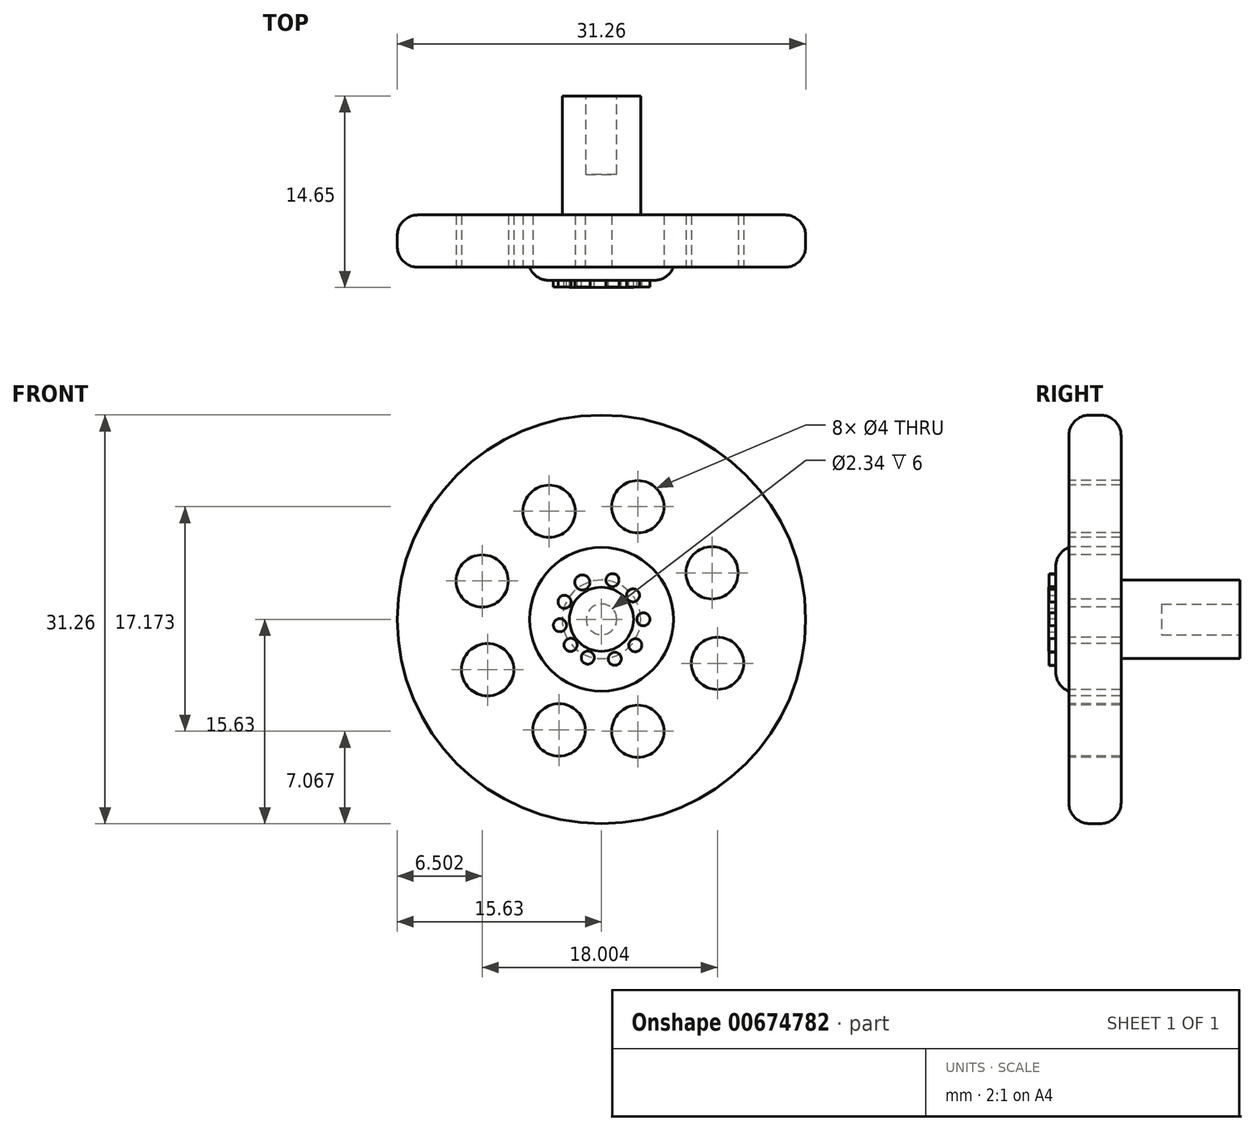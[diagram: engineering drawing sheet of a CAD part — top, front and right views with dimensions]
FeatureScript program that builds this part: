
annotation { "Feature Type Name" : "Feature", "Feature Type Description" : "" }
export const myFeature = defineFeature(function(context is Context, id is Id, definition is map)
    precondition{}
    {
        {
            var Q0;
            Q0=qCreatedBy(makeId("Front.planeOp"),FACE);
            var sketch = newSketch(context, id + "F0", { "sketchPlane" : qUnion([Q0])});
            skCircle(sketch, "E0", {"center": v(0, 0) * mm, "radius": 15.62 * mm});
            skSolve(sketch);
        }
        {
            var Q0;
            Q0 = qSketchRegion(id + "F0", true);
            extrude(context, id + "F1", {"entities" : qUnion([Q0]), "depth" : 4 * mm, "offsetDistance" : 25.4 * mm});
        }
        {
            var Q0;
            Q0=makeQuery(id+"F1.opExtrude","CAP_FACE",FACE,{"disambiguationData":[OSD([sQuery(id+"F0.wireOp",EDGE,"E0")])],"isStart":false});
            var sketch = newSketch(context, id + "F2", { "sketchPlane" : qUnion([Q0])});
            skCircle(sketch, "E1", {"center": v(0, 0) * mm, "radius": 2.45 * mm});
            skSolve(sketch);
        }
        {
            var Q0;
            Q0=makeQuery(id+"F2.imprint","IMPRINT",FACE,{"disambiguationData":[TD([[makeQuery(id+"F2.imprint","IMPRINT",EDGE,{"derivedFrom":sQuery(id+"F2.wireOp",EDGE,"E1")}),1.0]])]});
            extrude(context, id + "F3", {"entities" : qUnion([Q0]), "operationType" : NewBodyOperationType.ADD, "depth" : 1.55 * mm, "offsetDistance" : 25.4 * mm});
        }
        {
            var Q0;
            Q0=makeQuery(id+"F1.opExtrude","CAP_FACE",FACE,{"disambiguationData":[OSD([sQuery(id+"F0.wireOp",EDGE,"E0")])],"isStart":true});
            var sketch = newSketch(context, id + "F4", { "sketchPlane" : qUnion([Q0])});
            skCircle(sketch, "E2", {"center": v(0, 0) * mm, "radius": 3 * mm});
            skSolve(sketch);
        }
        {
            var Q0;
            Q0=makeQuery(id+"F4.imprint","IMPRINT",FACE,{"disambiguationData":[TD([[makeQuery(id+"F4.imprint","IMPRINT",EDGE,{"derivedFrom":sQuery(id+"F4.wireOp",EDGE,"E2")}),1.0]])]});
            extrude(context, id + "F5", {"entities" : qUnion([Q0]), "operationType" : NewBodyOperationType.ADD, "depth" : 9.1 * mm, "offsetDistance" : 25.4 * mm});
        }
        {
            var Q0;
            Q0=makeQuery(id+"F5.opExtrude","CAP_FACE",FACE,{"disambiguationData":[OSD([sQuery(id+"F4.wireOp",EDGE,"E2")])],"isStart":false});
            var sketch = newSketch(context, id + "F6", { "sketchPlane" : qUnion([Q0])});
            skCircle(sketch, "E3", {"center": v(0, 0) * mm, "radius": 1.17 * mm});
            skSolve(sketch);
        }
        {
            var Q0;
            Q0=makeQuery(id+"F6.imprint","IMPRINT",FACE,{"disambiguationData":[TD([[makeQuery(id+"F6.imprint","IMPRINT",EDGE,{"derivedFrom":sQuery(id+"F6.wireOp",EDGE,"E3")}),1.0]])]});
            var Q1;
            Q1=sQuery(id+"F6.wireOp",EDGE,"E3");
            extrude(context, id + "F7", {"entities" : qUnion([Q0]), "operationType" : NewBodyOperationType.REMOVE, "surfaceEntities" : qUnion([Q1]), "oppositeDirection" : true, "depth" : 6 * mm, "offsetDistance" : 25.4 * mm});
        }
        {
            var Q0;
            Q0=makeQuery(id+"F1.opExtrude","CAP_FACE",FACE,{"disambiguationData":[OSD([sQuery(id+"F0.wireOp",EDGE,"E0")])],"isStart":false});
            var sketch = newSketch(context, id + "F8", { "sketchPlane" : qUnion([Q0])});
            skCircle(sketch, "E4", {"center": v(0, 0) * mm, "radius": 5.5 * mm});
            skSolve(sketch);
        }
        {
            var Q0;
            Q0 = qSketchRegion(id + "F8", true);
            extrude(context, id + "F9", {"entities" : qUnion([Q0]), "operationType" : NewBodyOperationType.ADD, "depth" : 1 * mm, "offsetDistance" : 25.4 * mm});
        }
        {
            var Q0;
            Q0=makeQuery(id+"F1.opExtrude","CAP_EDGE",EDGE,{"disambiguationData":[OSD([sQuery(id+"F0.wireOp",EDGE,"E0")])],"isStart":false});
            var Q1;
            Q1=makeQuery(id+"F1.opExtrude","CAP_EDGE",EDGE,{"disambiguationData":[OSD([sQuery(id+"F0.wireOp",EDGE,"E0")])],"isStart":true});
            var Q2;
            Q2=makeQuery(id+"F9.opExtrude","CAP_EDGE",EDGE,{"disambiguationData":[OSD([sQuery(id+"F8.wireOp",EDGE,"E4")])],"isStart":false});
            fillet(context, id + "F10", {"entities" : qUnion([Q0, Q1, Q2]), "radius" : 1.58 * mm, "tangentPropagation" : true, "allowEdgeOverflow" : false});
        }
        {
            var Q0;
            Q0=makeQuery(id+"F9.opExtrude","CAP_FACE",FACE,{"disambiguationData":[OSD([sQuery(id+"F8.wireOp",EDGE,"E4")])],"isStart":false});
            var sketch = newSketch(context, id + "F11", { "sketchPlane" : qUnion([Q0])});
            skCircle(sketch, "E5", {"center": v(0.84, 3) * mm, "radius": 0.5 * mm});
            skCircle(sketch, "E6", {"center": v(2.41, 1.83) * mm, "radius": 0.5 * mm});
            skCircle(sketch, "E7", {"center": v(-2.83, 1.34) * mm, "radius": 0.5 * mm});
            skCircle(sketch, "E8", {"center": v(-3.18, -0.45) * mm, "radius": 0.5 * mm});
            skCircle(sketch, "E9", {"center": v(-2.36, -1.95) * mm, "radius": 0.5 * mm});
            skCircle(sketch, "E10", {"center": v(-1.05, -2.93) * mm, "radius": 0.5 * mm});
            skCircle(sketch, "E11", {"center": v(1.02, -3.02) * mm, "radius": 0.5 * mm});
            skCircle(sketch, "E12", {"center": v(-1.46, 2.82) * mm, "radius": 0.58 * mm});
            skCircle(sketch, "E13", {"center": v(2.59, -1.98) * mm, "radius": 0.5 * mm});
            skCircle(sketch, "E14", {"center": v(3.2, 0) * mm, "radius": 0.5 * mm});
            skSolve(sketch);
        }
        {
            var Q0;
            Q0=makeQuery(id+"F11.imprint","IMPRINT",FACE,{"disambiguationData":[TD([[makeQuery(id+"F11.imprint","IMPRINT",EDGE,{"derivedFrom":sQuery(id+"F11.wireOp",EDGE,"E7")}),1.0]])]});
            var Q1;
            Q1=makeQuery(id+"F11.imprint","IMPRINT",FACE,{"disambiguationData":[TD([[makeQuery(id+"F11.imprint","IMPRINT",EDGE,{"derivedFrom":sQuery(id+"F11.wireOp",EDGE,"E12")}),1.0]])]});
            var Q2;
            Q2=makeQuery(id+"F11.imprint","IMPRINT",FACE,{"disambiguationData":[TD([[makeQuery(id+"F11.imprint","IMPRINT",EDGE,{"derivedFrom":sQuery(id+"F11.wireOp",EDGE,"E6")}),1.0]])]});
            var Q3;
            Q3=makeQuery(id+"F11.imprint","IMPRINT",FACE,{"disambiguationData":[TD([[makeQuery(id+"F11.imprint","IMPRINT",EDGE,{"derivedFrom":sQuery(id+"F11.wireOp",EDGE,"E14")}),1.0]])]});
            var Q4;
            Q4=makeQuery(id+"F11.imprint","IMPRINT",FACE,{"disambiguationData":[TD([[makeQuery(id+"F11.imprint","IMPRINT",EDGE,{"derivedFrom":sQuery(id+"F11.wireOp",EDGE,"E13")}),1.0]])]});
            var Q5;
            Q5=makeQuery(id+"F11.imprint","IMPRINT",FACE,{"disambiguationData":[TD([[makeQuery(id+"F11.imprint","IMPRINT",EDGE,{"derivedFrom":sQuery(id+"F11.wireOp",EDGE,"E11")}),1.0]])]});
            var Q6;
            Q6=makeQuery(id+"F11.imprint","IMPRINT",FACE,{"disambiguationData":[TD([[makeQuery(id+"F11.imprint","IMPRINT",EDGE,{"derivedFrom":sQuery(id+"F11.wireOp",EDGE,"E10")}),1.0]])]});
            var Q7;
            Q7=makeQuery(id+"F11.imprint","IMPRINT",FACE,{"disambiguationData":[TD([[makeQuery(id+"F11.imprint","IMPRINT",EDGE,{"derivedFrom":sQuery(id+"F11.wireOp",EDGE,"E8")}),1.0]])]});
            var Q8;
            Q8=makeQuery(id+"F11.imprint","IMPRINT",FACE,{"disambiguationData":[TD([[makeQuery(id+"F11.imprint","IMPRINT",EDGE,{"derivedFrom":sQuery(id+"F11.wireOp",EDGE,"E5")}),1.0]])]});
            var Q9;
            Q9=makeQuery(id+"F11.imprint","IMPRINT",FACE,{"disambiguationData":[TD([[makeQuery(id+"F11.imprint","IMPRINT",EDGE,{"derivedFrom":sQuery(id+"F11.wireOp",EDGE,"E9")}),1.0]])]});
            extrude(context, id + "F12", {"entities" : qUnion([Q0, Q1, Q2, Q3, Q4, Q5, Q6, Q7, Q8, Q9]), "operationType" : NewBodyOperationType.ADD, "depth" : .5 * mm, "offsetDistance" : 25.4 * mm});
        }
        {
            var Q0;
            Q0=makeQuery(id+"F1.opExtrude","CAP_FACE",FACE,{"disambiguationData":[OSD([sQuery(id+"F0.wireOp",EDGE,"E0")])],"isStart":false});
            var sketch = newSketch(context, id + "F13", { "sketchPlane" : qUnion([Q0])});
            skCircle(sketch, "E15", {"center": v(2.78, 8.61) * mm, "radius": 2 * mm});
            skCircle(sketch, "E16", {"center": v(-4, 8.26) * mm, "radius": 2 * mm});
            skCircle(sketch, "E17", {"center": v(-9.13, 2.93) * mm, "radius": 2 * mm});
            skCircle(sketch, "E18", {"center": v(-8.71, -3.85) * mm, "radius": 2 * mm});
            skCircle(sketch, "E19", {"center": v(8.46, 3.56) * mm, "radius": 2 * mm});
            skCircle(sketch, "E20", {"center": v(8.88, -3.37) * mm, "radius": 2 * mm});
            skCircle(sketch, "E21", {"center": v(2.78, -8.56) * mm, "radius": 2 * mm});
            skCircle(sketch, "E22", {"center": v(-3.25, -8.46) * mm, "radius": 2 * mm});
            skSolve(sketch);
        }
        {
            var Q0;
            Q0=makeQuery(id+"F13.imprint","IMPRINT",FACE,{"disambiguationData":[TD([[makeQuery(id+"F13.imprint","IMPRINT",EDGE,{"derivedFrom":sQuery(id+"F13.wireOp",EDGE,"E16")}),1.0]])]});
            var Q1;
            Q1=makeQuery(id+"F13.imprint","IMPRINT",FACE,{"disambiguationData":[TD([[makeQuery(id+"F13.imprint","IMPRINT",EDGE,{"derivedFrom":sQuery(id+"F13.wireOp",EDGE,"E15")}),1.0]])]});
            var Q2;
            Q2=makeQuery(id+"F13.imprint","IMPRINT",FACE,{"disambiguationData":[TD([[makeQuery(id+"F13.imprint","IMPRINT",EDGE,{"derivedFrom":sQuery(id+"F13.wireOp",EDGE,"E17")}),1.0]])]});
            var Q3;
            Q3=makeQuery(id+"F13.imprint","IMPRINT",FACE,{"disambiguationData":[TD([[makeQuery(id+"F13.imprint","IMPRINT",EDGE,{"derivedFrom":sQuery(id+"F13.wireOp",EDGE,"E19")}),1.0]])]});
            var Q4;
            Q4=makeQuery(id+"F13.imprint","IMPRINT",FACE,{"disambiguationData":[TD([[makeQuery(id+"F13.imprint","IMPRINT",EDGE,{"derivedFrom":sQuery(id+"F13.wireOp",EDGE,"E20")}),1.0]])]});
            var Q5;
            Q5=makeQuery(id+"F13.imprint","IMPRINT",FACE,{"disambiguationData":[TD([[makeQuery(id+"F13.imprint","IMPRINT",EDGE,{"derivedFrom":sQuery(id+"F13.wireOp",EDGE,"E21")}),1.0]])]});
            var Q6;
            Q6=makeQuery(id+"F13.imprint","IMPRINT",FACE,{"disambiguationData":[TD([[makeQuery(id+"F13.imprint","IMPRINT",EDGE,{"derivedFrom":sQuery(id+"F13.wireOp",EDGE,"E22")}),1.0]])]});
            var Q7;
            Q7=makeQuery(id+"F13.imprint","IMPRINT",FACE,{"disambiguationData":[TD([[makeQuery(id+"F13.imprint","IMPRINT",EDGE,{"derivedFrom":sQuery(id+"F13.wireOp",EDGE,"E18")}),1.0]])]});
            extrude(context, id + "F14", {"entities" : qUnion([Q0, Q1, Q2, Q3, Q4, Q5, Q6, Q7]), "operationType" : NewBodyOperationType.REMOVE, "oppositeDirection" : true, "depth" : 25.4 * mm, "offsetDistance" : 25.4 * mm});
        }
    });
